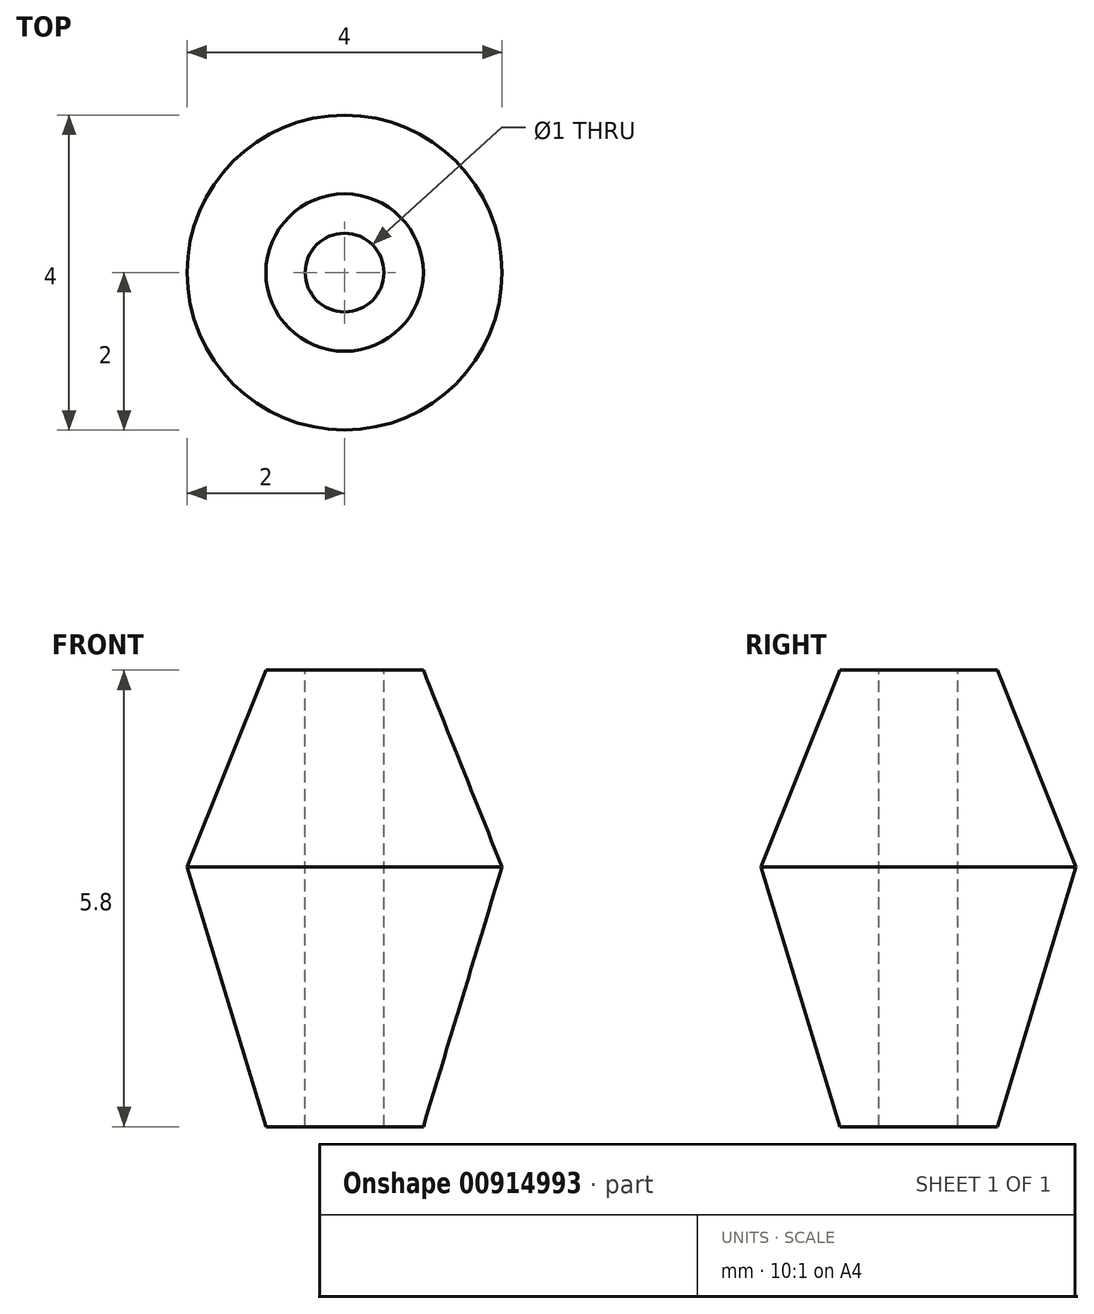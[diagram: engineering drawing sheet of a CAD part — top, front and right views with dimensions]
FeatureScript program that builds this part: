
annotation { "Feature Type Name" : "Feature", "Feature Type Description" : "" }
export const myFeature = defineFeature(function(context is Context, id is Id, definition is map)
    precondition{}
    {
        {
            var Q0;
            Q0=qCreatedBy(makeId("Front.planeOp"),FACE);
            var sketch = newSketch(context, id + "F0", { "sketchPlane" : qUnion([Q0])});
            skLineSegment(sketch, "E0", {"start": v(0, 0) * mm, "end": v(1, 2.5) * mm});
            skLineSegment(sketch, "E1", {"start": v(1, 2.5) * mm, "end": v(1, 0) * mm});
            skLineSegment(sketch, "E2", {"start": v(1, -3.3) * mm, "end": v(1, 0) * mm});
            skLineSegment(sketch, "E3", {"start": v(2, 2.5) * mm, "end": v(2, -3.3) * mm});
            skLineSegment(sketch, "E4", {"start": v(2, 2.5) * mm, "end": v(1, 2.5) * mm});
            skLineSegment(sketch, "E5", {"start": v(2, -3.3) * mm, "end": v(1, -3.3) * mm});
            skLineSegment(sketch, "E6", {"start": v(0, 0) * mm, "end": v(1, 0) * mm});
            skLineSegment(sketch, "E7", {"start": v(0, 0) * mm, "end": v(1, -3.3) * mm});
            skSolve(sketch);
        }
        {
            var Q0;
            Q0=makeQuery(id+"F0.imprint","IMPRINT",FACE,{"disambiguationData":[TD([[makeQuery(id+"F0.imprint","IMPRINT",EDGE,{"derivedFrom":sQuery(id+"F0.wireOp",EDGE,"E0")}),-1.0]])]});
            var Q1;
            Q1=makeQuery(id+"F0.imprint","IMPRINT",FACE,{"disambiguationData":[TD([[makeQuery(id+"F0.imprint","IMPRINT",EDGE,{"derivedFrom":sQuery(id+"F0.wireOp",EDGE,"E1")}),1.0]])]});
            var Q2;
            Q2=makeQuery(id+"F0.imprint","IMPRINT",FACE,{"disambiguationData":[TD([[makeQuery(id+"F0.imprint","IMPRINT",EDGE,{"derivedFrom":sQuery(id+"F0.wireOp",EDGE,"E2")}),1.0]])]});
            var Q3;
            Q3=sQuery(id+"F0.wireOp",EDGE,"E3");
            revolve(context, id + "F1", {"surfaceOperationType" : NewSurfaceOperationType.NEW, "entities" : qUnion([Q0, Q1, Q2]), "axis" : qUnion([Q3]), "revolveType" : RevolveType.FULL});
        }
        {
            var Q0;
            Q0=makeQuery(id+"F1.opRevolve","SWEPT_FACE",FACE,{"disambiguationData":[OSD([sQuery(id+"F0.wireOp",EDGE,"E4")])]});
            var sketch = newSketch(context, id + "F2", { "sketchPlane" : qUnion([Q0])});
            skPoint(sketch, "E8", {"position": v(2, 0) * mm});
            skSolve(sketch);
        }
        {
            var Q0;
            Q0=sQuery(id+"F2.wireOp",VERTEX,"E8");
            var Q1;
            Q1=makeQuery(id+"F1.opRevolve","SWEPT_BODY",BODY,{"disambiguationData":[OSD([sQuery(id+"F0.wireOp",EDGE,"E0"),sQuery(id+"F0.wireOp",EDGE,"E3"),sQuery(id+"F0.wireOp",EDGE,"E4"),sQuery(id+"F0.wireOp",EDGE,"E5"),sQuery(id+"F0.wireOp",EDGE,"E7")])]});
            hole(context, id + "F3", {"style" : HoleStyle.SIMPLE, "endStyle" : HoleEndStyle.THROUGH, "holeDiameter" : 1 * mm, "majorDiameter" : 6.35 * mm, "isTappedThrough" : true, "tappedDepth" : 12.7 * mm, "tapClearance" : 3, "locations" : qUnion([Q0]), "scope" : qUnion([Q1])});
        }
    });
